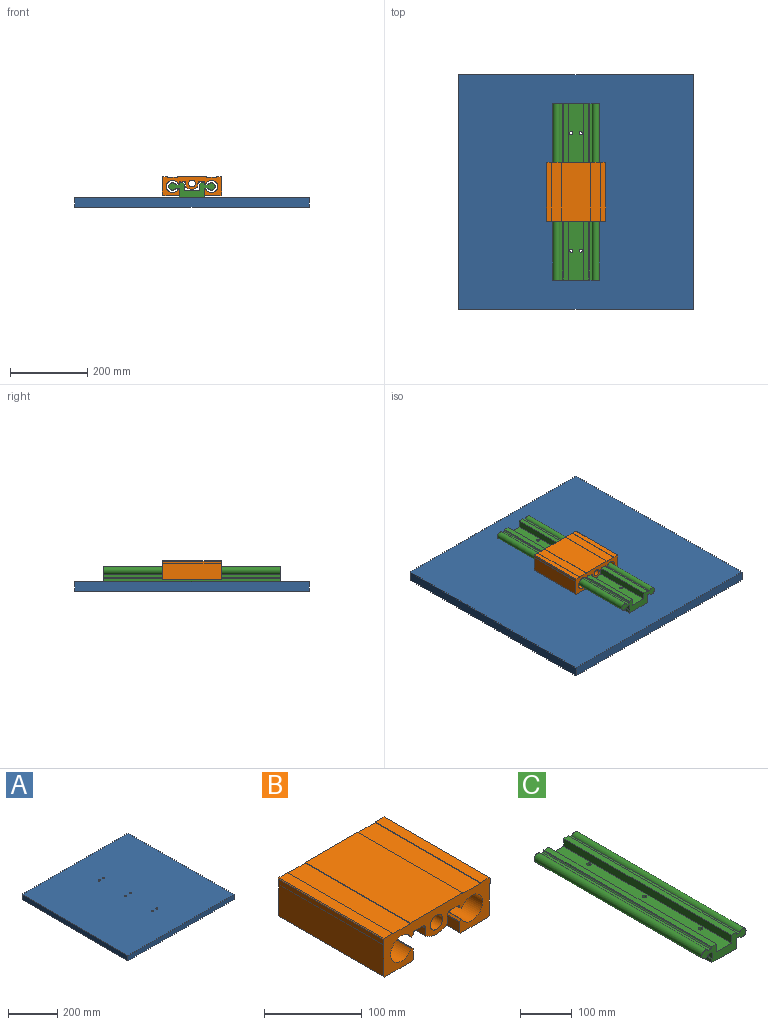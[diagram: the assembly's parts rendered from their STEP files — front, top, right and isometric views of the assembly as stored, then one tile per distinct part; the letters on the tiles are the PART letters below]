
ASSEMBLY  parts=3 mates=2
PART A: 12 faces, bbox 609.6x609.6x25.4 mm
  f0: plane 609.6x25.4mm, normal (0,-1,0), area 15483.8mm2, adj f1,f9,f10,f11
  f1: plane 609.6x25.4mm, normal (1,0,0), area 15483.8mm2, adj f0,f2,f10,f11
  f2: plane 609.6x25.4mm, normal (0,1,0), area 15483.8mm2, adj f1,f9,f10,f11
  f3: cylinder r=4.32mm len=25.4mm, axis (0,0,1), area 689.1mm2, adj f10,f11
  f4: cylinder r=4.32mm len=25.4mm, axis (0,0,1), area 689.1mm2, adj f10,f11
  f5: cylinder r=4.32mm len=25.4mm, axis (0,0,1), area 689.1mm2, adj f10,f11
  f6: cylinder r=4.32mm len=25.4mm, axis (0,0,1), area 689.1mm2, adj f10,f11
  f7: cylinder r=4.32mm len=25.4mm, axis (0,0,1), area 689.1mm2, adj f10,f11
  f8: cylinder r=4.32mm len=25.4mm, axis (0,0,1), area 689.1mm2, adj f10,f11
  f9: plane 609.6x25.4mm, normal (-1,0,0), area 15483.8mm2, adj f0,f2,f10,f11
  f10: plane 609.6x609.6mm, normal (0,0,-1), area 371260.7mm2, adj f0,f1,f2,f3,f4,f5,f6,f7
  f11: plane 609.6x609.6mm, normal (0,0,1), area 371260.7mm2, adj f0,f1,f2,f3,f4,f5,f6,f7
PART B: 53 faces, bbox 154.9x152.4x49 mm
  f0: plane 152.4x9.66mm, normal (-1,0,0), area 1472.8mm2, adj f1,f33,f34,f36
  f1: cylinder r=25.4mm len=152.4mm, axis (0,1,0), area 5103.6mm2, adj f0,f2,f33,f34
  f2: plane 152.4x9.66mm, normal (1,0,0), area 1472.8mm2, adj f1,f33,f34,f35
  f3: plane 152.4x10.48mm, normal (0,0,-1), area 1596.8mm2, adj f33,f34,f35,f37
  f4: plane 152.4x0.95mm, normal (-1,0,0), area 145mm2, adj f33,f34,f37,f39
  f5: plane 152.4x1.77mm, normal (-0.71,0,-0.71), area 381.6mm2, adj f33,f34,f39,f40
  f6: cylinder r=15.88mm len=152.4mm, axis (0,1,0), area 12939.9mm2, adj f33,f34,f40,f41
  f7: plane 152.4x1.77mm, normal (-0.71,0,0.71), area 381.6mm2, adj f33,f34,f41,f42
  f8: plane 152.4x13.14mm, normal (-1,0,0), area 2003.1mm2, adj f33,f34,f42,f50
  f9: plane 152.4x40.51mm, normal (0,0,-1), area 6174.2mm2, adj f33,f34,f49,f50
  f10: plane 152.4x40.13mm, normal (1,0,0), area 6116.1mm2, adj f11,f33,f34,f49
  f11: plane 152.4x0.76mm, normal (0,0,-1), area 116.1mm2, adj f10,f12,f33,f34
  f12: plane 152.4x6.35mm, normal (1,0,0), area 967.7mm2, adj f11,f33,f34,f47
  f13: plane 152.4x12.7mm, normal (0,0,1), area 1935.5mm2, adj f14,f33,f34,f47
  f14: plane 152.4x0.76mm, normal (-1,0,0), area 116.1mm2, adj f13,f15,f33,f34
  f15: plane 152.4x25.4mm, normal (0,0,1), area 3871mm2, adj f14,f16,f33,f34
  f16: plane 152.4x0.76mm, normal (1,0,0), area 116.1mm2, adj f15,f17,f33,f34
  f17: plane 152.4x76.2mm, normal (0,0,1), area 11612.9mm2, adj f16,f18,f33,f34
  f18: plane 152.4x0.76mm, normal (-1,0,0), area 116.1mm2, adj f17,f19,f33,f34
  f19: plane 152.4x25.4mm, normal (0,0,1), area 3871mm2, adj f18,f20,f33,f34
  f20: plane 152.4x0.76mm, normal (1,0,0), area 116.1mm2, adj f19,f21,f33,f34
  f21: plane 152.4x12.7mm, normal (0,0,1), area 1935.5mm2, adj f20,f33,f34,f48
  f22: plane 152.4x6.35mm, normal (-1,0,0), area 967.7mm2, adj f23,f33,f34,f48
  f23: plane 152.4x0.76mm, normal (0,0,-1), area 116.1mm2, adj f22,f24,f33,f34
  f24: plane 152.4x40.13mm, normal (-1,0,0), area 6116.1mm2, adj f23,f33,f34,f52
  f25: plane 152.4x40.51mm, normal (0,0,-1), area 6174.2mm2, adj f33,f34,f51,f52
  f26: plane 152.4x13.14mm, normal (1,0,0), area 2003.1mm2, adj f33,f34,f43,f51
  f27: plane 152.4x1.77mm, normal (0.71,0,0.71), area 381.6mm2, adj f33,f34,f43,f44
  f28: cylinder r=15.88mm len=152.4mm, axis (0,1,0), area 12939.9mm2, adj f33,f34,f44,f45
  f29: plane 152.4x1.77mm, normal (0.71,0,-0.71), area 381.6mm2, adj f33,f34,f45,f46
  f30: plane 152.4x0.95mm, normal (1,0,0), area 145mm2, adj f33,f34,f38,f46
  f31: cylinder r=8.89mm len=152.4mm, axis (0,1,0), area 8512.7mm2, adj f33,f34
  f32: plane 152.4x10.48mm, normal (0,0,-1), area 1596.8mm2, adj f33,f34,f36,f38
  f33: plane 154.94x49.02mm, normal (0,-1,0), area 3740.3mm2, adj f0,f1,f2,f3,f4,f5,f6,f7
  f34: plane 154.94x49.02mm, normal (0,1,0), area 3740.3mm2, adj f0,f1,f2,f3,f4,f5,f6,f7
  f35: cylinder r=5.08mm len=152.4mm, axis (0,1,0), area 1216.1mm2, adj f2,f3,f33,f34
  f36: cylinder r=5.08mm len=152.4mm, axis (0,-1,0), area 1216.1mm2, adj f0,f32,f33,f34
  f37: cylinder r=2.54mm len=152.4mm, axis (0,1,0), area 608mm2, adj f3,f4,f33,f34
  f38: cylinder r=2.54mm len=152.4mm, axis (0,-1,0), area 608mm2, adj f30,f32,f33,f34
  f39: cylinder r=0.64mm len=152.4mm, axis (0,1,0), area 76mm2, adj f4,f5,f33,f34
  f40: cylinder r=0.64mm len=152.4mm, axis (0,1,0), area 182.8mm2, adj f5,f6,f33,f34
  f41: cylinder r=0.64mm len=152.4mm, axis (0,1,0), area 182.8mm2, adj f6,f7,f33,f34
  f42: cylinder r=0.64mm len=152.4mm, axis (0,1,0), area 76mm2, adj f7,f8,f33,f34
  f43: cylinder r=0.64mm len=152.4mm, axis (0,1,0), area 76mm2, adj f26,f27,f33,f34
  f44: cylinder r=0.64mm len=152.4mm, axis (0,1,0), area 182.8mm2, adj f27,f28,f33,f34
  f45: cylinder r=0.64mm len=152.4mm, axis (0,1,0), area 182.8mm2, adj f28,f29,f33,f34
  f46: cylinder r=0.64mm len=152.4mm, axis (0,1,0), area 76mm2, adj f29,f30,f33,f34
  f47: plane 152.4x1.27mm, normal (0.71,0,0.71), area 273.7mm2, adj f12,f13,f33,f34
  f48: plane 152.4x1.27mm, normal (-0.71,0,0.71), area 273.7mm2, adj f21,f22,f33,f34
  f49: plane 152.4x1.27mm, normal (0.71,0,-0.71), area 273.7mm2, adj f9,f10,f33,f34
  f50: plane 152.4x1.27mm, normal (-0.71,0,-0.71), area 273.7mm2, adj f8,f9,f33,f34
  f51: plane 152.4x1.27mm, normal (0.71,0,-0.71), area 273.7mm2, adj f25,f26,f33,f34
  f52: plane 152.4x1.27mm, normal (-0.71,0,-0.71), area 273.7mm2, adj f24,f25,f33,f34
PART C: 31 faces, bbox 120.7x457.2x38.1 mm
  f0: plane 457.2x6.68mm, normal (0,0,1), area 3054.2mm2, adj f1,f18,f19,f24
  f1: cylinder r=9.53mm len=457.2mm, axis (0,1,0), area 22813mm2, adj f0,f2,f18,f19
  f2: plane 457.2x7.95mm, normal (0,0,-1), area 3634.8mm2, adj f1,f18,f19,f21
  f3: plane 457.2x11.89mm, normal (-1,0,0), area 5433.9mm2, adj f4,f18,f19,f21
  f4: plane 457.2x1.27mm, normal (-0.71,0,0.71), area 821.2mm2, adj f3,f5,f18,f19
  f5: plane 457.2x7.32mm, normal (-1,0,0), area 3344.5mm2, adj f4,f18,f19,f20
  f6: plane 457.2x65.99mm, normal (0,0,-1), area 29818.8mm2, adj f7,f18,f19,f20,f25,f26,f27,f28
  f7: plane 457.2x21.28mm, normal (1,0,0), area 9730.6mm2, adj f6,f18,f19,f22
  f8: plane 457.2x6.53mm, normal (0,0,-1), area 2984.5mm2, adj f9,f18,f19,f22
  f9: cylinder r=9.53mm len=457.2mm, axis (0,1,0), area 22813mm2, adj f8,f10,f18,f19
  f10: plane 457.2x6.53mm, normal (0,0,1), area 2984.5mm2, adj f9,f18,f19,f23
  f11: plane 457.2x1.86mm, normal (1,0,0), area 849.1mm2, adj f12,f18,f19,f23
  f12: plane 457.2x12.83mm, normal (0,0,1), area 5864.5mm2, adj f11,f13,f18,f19
  f13: plane 457.2x18.67mm, normal (-1,0,0), area 8537.8mm2, adj f12,f14,f18,f19
  f14: plane 457.2x41.15mm, normal (0,0,1), area 18461.4mm2, adj f13,f15,f18,f19,f25,f26,f27,f28
  f15: plane 457.2x18.67mm, normal (1,0,0), area 8537.8mm2, adj f14,f16,f18,f19
  f16: plane 457.2x12.83mm, normal (0,0,1), area 5864.5mm2, adj f15,f17,f18,f19
  f17: plane 457.2x1.86mm, normal (-1,0,0), area 849.1mm2, adj f16,f18,f19,f24
  f18: plane 120.65x38.1mm, normal (0,-1,0), area 2465.3mm2, adj f0,f1,f2,f3,f4,f5,f6,f7
  f19: plane 120.65x38.1mm, normal (0,1,0), area 2465.3mm2, adj f0,f1,f2,f3,f4,f5,f6,f7
  f20: plane 457.2x0.81mm, normal (-0.71,0,-0.71), area 525.5mm2, adj f5,f6,f18,f19
  f21: cylinder r=2.54mm len=457.2mm, axis (0,-1,0), area 1824.1mm2, adj f2,f3,f18,f19
  f22: cylinder r=2.54mm len=457.2mm, axis (0,-1,0), area 1824.1mm2, adj f7,f8,f18,f19
  f23: cylinder r=2.54mm len=457.2mm, axis (0,-1,0), area 1824.1mm2, adj f10,f11,f18,f19
  f24: cylinder r=2.54mm len=457.2mm, axis (0,-1,0), area 1824.1mm2, adj f0,f17,f18,f19
  f25: cylinder r=4.32mm len=19.05mm, axis (0,0,1), area 516.8mm2, adj f6,f14
  f26: cylinder r=4.32mm len=19.05mm, axis (0,0,1), area 516.8mm2, adj f6,f14
  f27: cylinder r=4.32mm len=19.05mm, axis (0,0,1), area 516.8mm2, adj f6,f14
  f28: cylinder r=4.32mm len=19.05mm, axis (0,0,1), area 516.8mm2, adj f6,f14
  f29: cylinder r=4.32mm len=19.05mm, axis (0,0,1), area 516.8mm2, adj f6,f14
  f30: cylinder r=4.32mm len=19.05mm, axis (0,0,1), area 516.8mm2, adj f6,f14
PLACE A at identity fixed
PLACE B t=(0,0.36,0)mm
PLACE C at identity
MATE fastened C.f26 <-> A.f6  axis (0,0,-1) through (12.7,-152.4,0)mm
MATE slider B.f6 <-> C.f9  axis (0,1,0) through (50.72,0.36,28.58)mm
